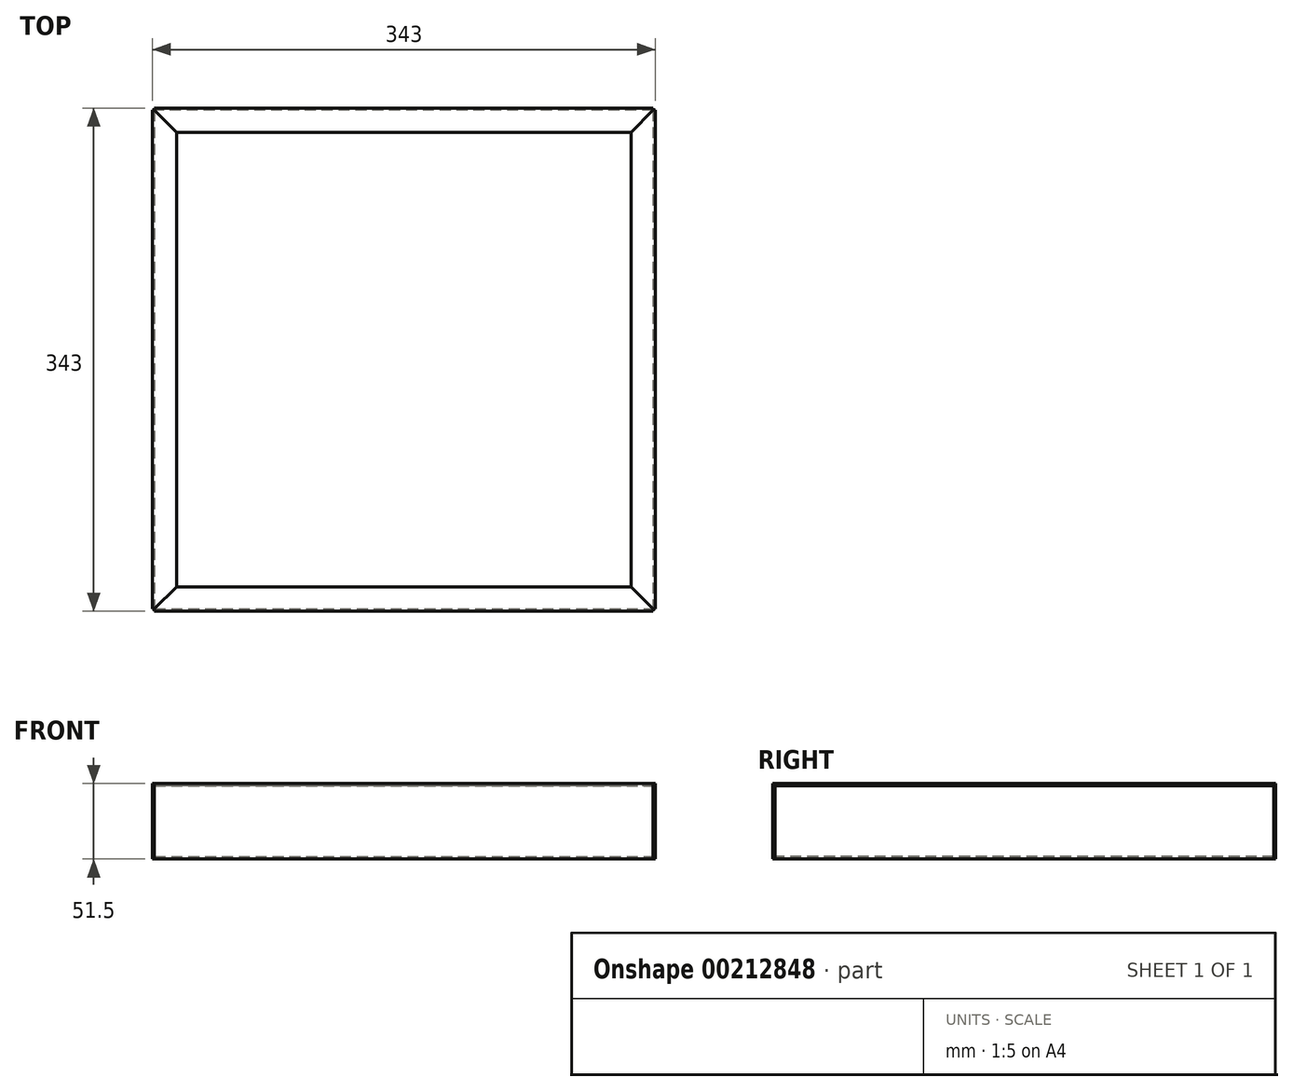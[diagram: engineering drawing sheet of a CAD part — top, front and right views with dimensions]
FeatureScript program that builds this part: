
annotation { "Feature Type Name" : "Feature", "Feature Type Description" : "" }
export const myFeature = defineFeature(function(context is Context, id is Id, definition is map)
    precondition{}
    {
        {
            var Q0;
            Q0=qCreatedBy(makeId("Top.planeOp"),FACE);
            var sketch = newSketch(context, id + "F0", { "sketchPlane" : qUnion([Q0])});
            skLineSegment(sketch, "E0.bottom", {"start": v(-170, 170) * mm, "end": v(170, 170) * mm});
            skLineSegment(sketch, "E0.top", {"start": v(-170, -170) * mm, "end": v(170, -170) * mm});
            skLineSegment(sketch, "E0.left", {"start": v(-170, 170) * mm, "end": v(-170, -170) * mm});
            skLineSegment(sketch, "E0.right", {"start": v(170, 170) * mm, "end": v(170, -170) * mm});
            skSolve(sketch);
        }
        {
            var Q0;
            Q0 = qSketchRegion(id + "F0", true);
            extrude(context, id + "F1", {"entities" : qUnion([Q0]), "depth" : 1.5 * mm});
        }
        {
            var Q0;
            Q0=makeQuery(id+"F1.opExtrude","SWEPT_FACE",FACE,{"disambiguationData":[OSD([sQuery(id+"F0.wireOp",EDGE,"E0.top")])]});
            var sketch = newSketch(context, id + "F2", { "sketchPlane" : qUnion([Q0])});
            skLineSegment(sketch, "E1.bottom", {"start": v(-170, 0) * mm, "end": v(170, 0) * mm});
            skLineSegment(sketch, "E1.top", {"start": v(-170, 50) * mm, "end": v(170, 50) * mm});
            skLineSegment(sketch, "E1.left", {"start": v(-170, 0) * mm, "end": v(-170, 50) * mm});
            skLineSegment(sketch, "E1.right", {"start": v(170, 0) * mm, "end": v(170, 50) * mm});
            skSolve(sketch);
        }
        {
            var Q0;
            Q0 = qSketchRegion(id + "F2", true);
            extrude(context, id + "F3", {"entities" : qUnion([Q0]), "depth" : 1.5 * mm});
        }
        {
            var Q0;
            Q0=makeQuery(id+"F1.opExtrude","CAP_FACE",FACE,{"disambiguationData":[OSD([sQuery(id+"F0.wireOp",EDGE,"E0.bottom"),sQuery(id+"F0.wireOp",EDGE,"E0.top"),sQuery(id+"F0.wireOp",EDGE,"E0.left"),sQuery(id+"F0.wireOp",EDGE,"E0.right")])],"isStart":false});
            var sketch = newSketch(context, id + "F4", { "sketchPlane" : qUnion([Q0])});
            skCircle(sketch, "E2", {"center": v(0, 0) * mm, "radius": 170 * mm, "construction": true});
            skSolve(sketch);
        }
        {
            var Q0;
            Q0=makeQuery(id+"F3.opExtrude","SWEPT_BODY",BODY,{"disambiguationData":[OSD([sQuery(id+"F2.wireOp",EDGE,"E1.bottom"),sQuery(id+"F2.wireOp",EDGE,"E1.top"),sQuery(id+"F2.wireOp",EDGE,"E1.left"),sQuery(id+"F2.wireOp",EDGE,"E1.right")])]});
            var Q1;
            Q1=sQuery(id+"F4.wireOp",EDGE,"E2");
            circularPattern(context, id + "F5", {"entities" : qUnion([Q0]), "axis" : qUnion([Q1]), "angle" : 360 * degree, "instanceCount" : 4, "equalSpace" : true});
        }
        {
            var Q0;
            Q0=makeQuery(id+"F3.opExtrude","SWEPT_FACE",FACE,{"disambiguationData":[OSD([sQuery(id+"F2.wireOp",EDGE,"E1.top")])]});
            var sketch = newSketch(context, id + "F6", { "sketchPlane" : qUnion([Q0])});
            skLineSegment(sketch, "E3", {"start": v(-170, -171.5) * mm, "end": v(170, -171.5) * mm});
            skLineSegment(sketch, "E4", {"start": v(155, -155) * mm, "end": v(-155, -155) * mm});
            skLineSegment(sketch, "E5", {"start": v(-155, -155) * mm, "end": v(-170, -170) * mm});
            skLineSegment(sketch, "E6", {"start": v(-170, -170) * mm, "end": v(-170, -171.5) * mm});
            skLineSegment(sketch, "E7", {"start": v(170, -171.5) * mm, "end": v(170, -170) * mm});
            skLineSegment(sketch, "E8", {"start": v(170, -170) * mm, "end": v(155, -155) * mm});
            skLineSegment(sketch, "E9", {"start": v(155, -155) * mm, "end": v(155, -170) * mm, "construction": true});
            skLineSegment(sketch, "E10", {"start": v(-155, -155) * mm, "end": v(-155, -170) * mm, "construction": true});
            skSolve(sketch);
        }
        {
            var Q0;
            Q0 = qSketchRegion(id + "F6", true);
            extrude(context, id + "F7", {"entities" : qUnion([Q0]), "operationType" : NewBodyOperationType.ADD, "depth" : 1.5 * mm});
        }
        {
            var Q0;
            Q0=makeQuery(id+"F3.opExtrude","SWEPT_BODY",BODY,{"disambiguationData":[OSD([sQuery(id+"F2.wireOp",EDGE,"E1.bottom"),sQuery(id+"F2.wireOp",EDGE,"E1.top"),sQuery(id+"F2.wireOp",EDGE,"E1.left"),sQuery(id+"F2.wireOp",EDGE,"E1.right")])]});
            var Q1;
            Q1=sQuery(id+"F4.wireOp",EDGE,"E2");
            circularPattern(context, id + "F8", {"entities" : qUnion([Q0]), "axis" : qUnion([Q1]), "angle" : 360 * degree, "instanceCount" : 4, "equalSpace" : true});
        }
    });
